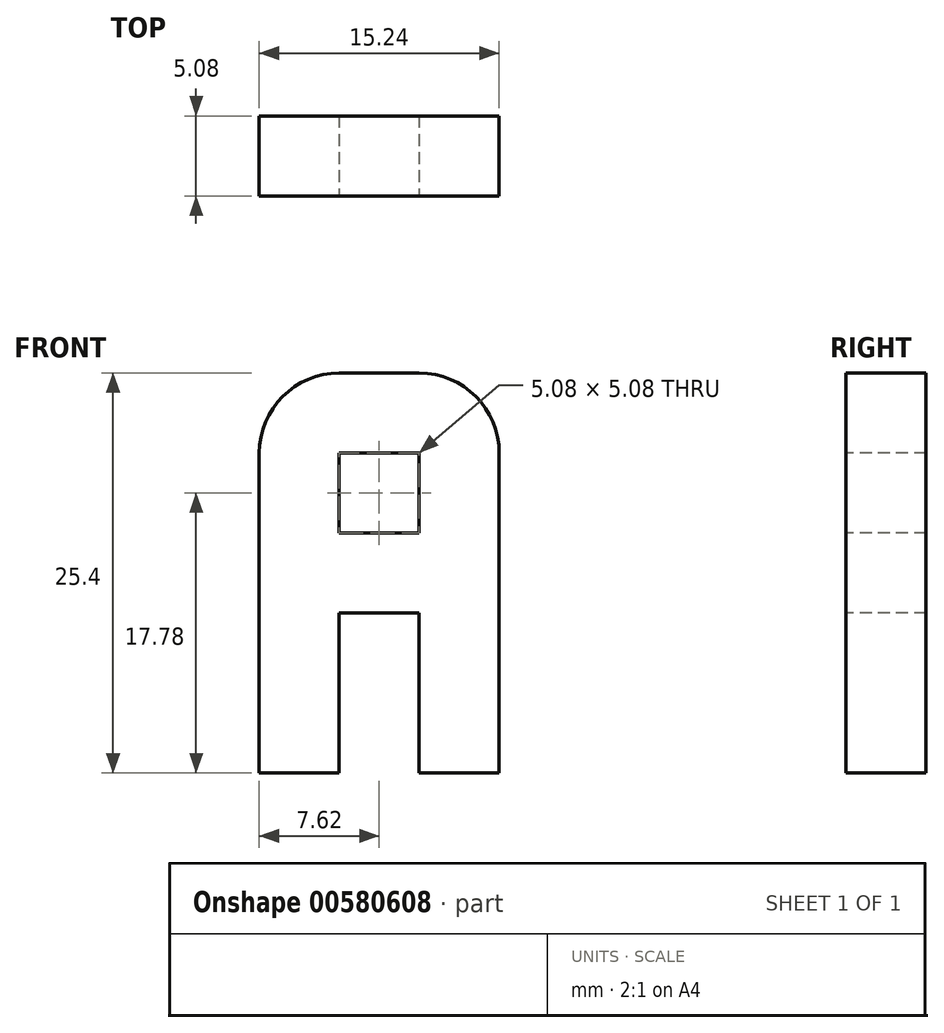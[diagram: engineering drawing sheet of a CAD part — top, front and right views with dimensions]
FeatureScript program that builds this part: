
annotation { "Feature Type Name" : "Feature", "Feature Type Description" : "" }
export const myFeature = defineFeature(function(context is Context, id is Id, definition is map)
    precondition{}
    {
        {
            var Q0;
            Q0=qCreatedBy(makeId("Front.planeOp"),FACE);
            var sketch = newSketch(context, id + "F0", { "sketchPlane" : qUnion([Q0])});
            skLineSegment(sketch, "E0.bottom", {"start": v(7.62, 12.7) * mm, "end": v(-7.62, 12.7) * mm});
            skLineSegment(sketch, "E0.top", {"start": v(7.62, -12.7) * mm, "end": v(-7.62, -12.7) * mm});
            skLineSegment(sketch, "E0.left", {"start": v(7.62, 12.7) * mm, "end": v(7.62, -12.7) * mm});
            skLineSegment(sketch, "E0.right", {"start": v(-7.62, 12.7) * mm, "end": v(-7.62, -12.7) * mm});
            skPoint(sketch, "E0.middle", {"position": v(0, 0) * mm});
            skSolve(sketch);
        }
        {
            var Q0;
            Q0=makeQuery(id+"F0.imprint","IMPRINT",FACE,{"disambiguationData":[TD([[makeQuery(id+"F0.imprint","IMPRINT",EDGE,{"derivedFrom":sQuery(id+"F0.wireOp",EDGE,"E0.bottom")}),1.0]])]});
            extrude(context, id + "F1", {"entities" : qUnion([Q0]), "depth" : 5.08 * mm, "offsetDistance" : 25.4 * mm});
        }
        {
            var Q0;
            Q0=makeQuery(id+"F1.opExtrude","CAP_FACE",FACE,{"disambiguationData":[OSD([sQuery(id+"F0.wireOp",EDGE,"E0.bottom"),sQuery(id+"F0.wireOp",EDGE,"E0.top"),sQuery(id+"F0.wireOp",EDGE,"E0.left"),sQuery(id+"F0.wireOp",EDGE,"E0.right")])],"isStart":false});
            var sketch = newSketch(context, id + "F2", { "sketchPlane" : qUnion([Q0])});
            skLineSegment(sketch, "E1.bottom", {"start": v(-2.54, -12.7) * mm, "end": v(2.54, -12.7) * mm});
            skLineSegment(sketch, "E1.top", {"start": v(-2.54, -2.54) * mm, "end": v(2.54, -2.54) * mm});
            skLineSegment(sketch, "E1.left", {"start": v(-2.54, -12.7) * mm, "end": v(-2.54, -2.54) * mm});
            skLineSegment(sketch, "E1.right", {"start": v(2.54, -12.7) * mm, "end": v(2.54, -2.54) * mm});
            skLineSegment(sketch, "E2.bottom", {"start": v(-2.54, 7.62) * mm, "end": v(2.54, 7.62) * mm});
            skLineSegment(sketch, "E2.top", {"start": v(-2.54, 2.54) * mm, "end": v(2.54, 2.54) * mm});
            skLineSegment(sketch, "E2.left", {"start": v(-2.54, 7.62) * mm, "end": v(-2.54, 2.54) * mm});
            skLineSegment(sketch, "E2.right", {"start": v(2.54, 7.62) * mm, "end": v(2.54, 2.54) * mm});
            skSolve(sketch);
        }
        {
            var Q0;
            Q0=makeQuery(id+"F2.imprint","IMPRINT",FACE,{"disambiguationData":[TD([[makeQuery(id+"F2.imprint","IMPRINT",EDGE,{"derivedFrom":sQuery(id+"F2.wireOp",EDGE,"E2.bottom")}),-1.0]])]});
            var Q1;
            Q1=makeQuery(id+"F2.imprint","IMPRINT",FACE,{"disambiguationData":[TD([[makeQuery(id+"F2.imprint","IMPRINT",EDGE,{"derivedFrom":sQuery(id+"F2.wireOp",EDGE,"E1.bottom")}),-1.0]])]});
            extrude(context, id + "F3", {"entities" : qUnion([Q0, Q1]), "operationType" : NewBodyOperationType.REMOVE, "oppositeDirection" : true, "depth" : 5.08 * mm, "offsetDistance" : 25.4 * mm});
        }
        {
            var Q0;
            Q0=makeQuery(id+"F1.opExtrude","SWEPT_EDGE",EDGE,{"disambiguationData":[OSD([sQuery(id+"F0.wireOp",EDGE,"E0.bottom"),sQuery(id+"F0.wireOp",EDGE,"E0.right")])]});
            var Q1;
            Q1=makeQuery(id+"F1.opExtrude","SWEPT_EDGE",EDGE,{"disambiguationData":[OSD([sQuery(id+"F0.wireOp",EDGE,"E0.bottom"),sQuery(id+"F0.wireOp",EDGE,"E0.left")])]});
            fillet(context, id + "F4", {"entities" : qUnion([Q0, Q1]), "radius" : 5.08 * mm, "tangentPropagation" : true, "allowEdgeOverflow" : false});
        }
    });
